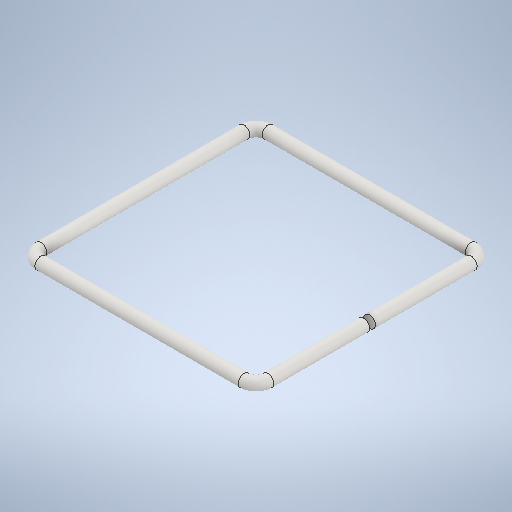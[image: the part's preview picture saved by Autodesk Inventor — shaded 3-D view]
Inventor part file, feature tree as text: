
AUTODESK INVENTOR PART (.ipt)
format: ipt  version: 2025.1 (Build 291241020, 241B)  size: 290,304 bytes
history: native  units: in
note: dims shown in document units (in); Inventor stores cm internally (conversion verified against a paired STEP export)
features: sketch x2, sweep x1
ambient origin geometry x8: Origin, YZ Plane, XZ Plane, XY Plane, X Axis, Y Axis, Z Axis, Center Point
bodies: Solid1 (feature_tree)
feature tree (3):
  sweep  "Sweep1"
  sketch  "Sketch1"  dims[d0=0.5in d1=0.25in]
  sketch  "Sketch2"  dims[d2=4.75in d3=9.5in d4=9.5in d8=0.5in d9=0.0in d10=0.0in]
